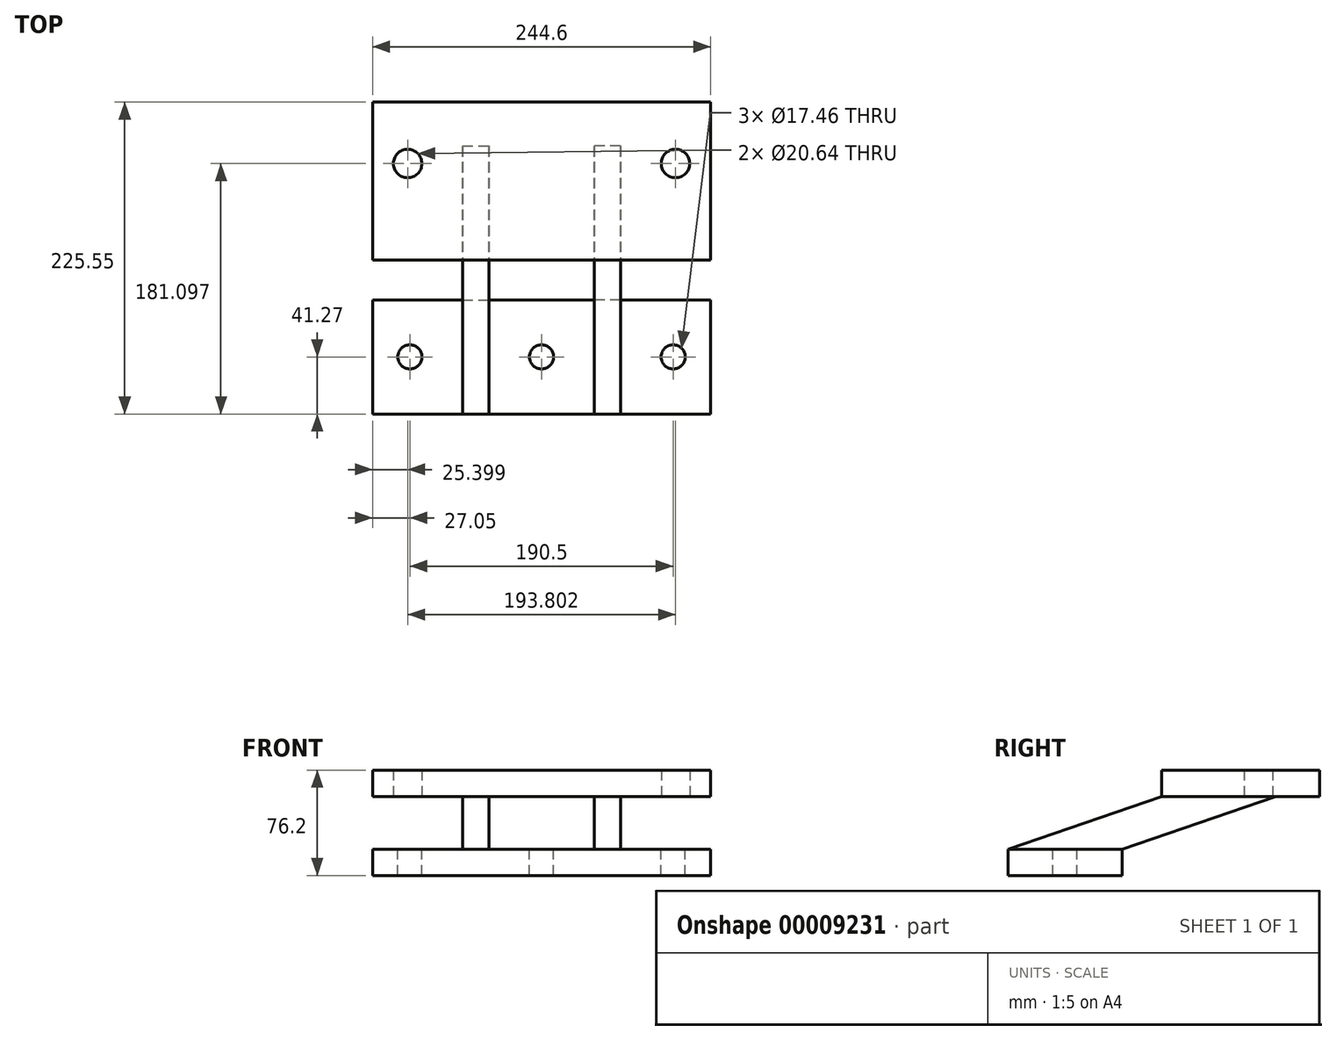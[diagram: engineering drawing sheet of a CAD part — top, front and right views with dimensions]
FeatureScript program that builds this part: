
annotation { "Feature Type Name" : "Feature", "Feature Type Description" : "" }
export const myFeature = defineFeature(function(context is Context, id is Id, definition is map)
    precondition{}
    {
        {
            var Q0;
            Q0=qCreatedBy(makeId("Top.planeOp"),FACE);
            var sketch = newSketch(context, id + "F0", { "sketchPlane" : qUnion([Q0])});
            skLineSegment(sketch, "E0.rect.bottom", {"start": v(-122.3, 41.28) * mm, "end": v(122.3, 41.28) * mm});
            skLineSegment(sketch, "E0.rect.top", {"start": v(-122.3, -41.28) * mm, "end": v(122.3, -41.28) * mm});
            skLineSegment(sketch, "E0.rect.left", {"start": v(-122.3, 41.28) * mm, "end": v(-122.3, -41.28) * mm});
            skLineSegment(sketch, "E0.rect.right", {"start": v(122.3, 41.28) * mm, "end": v(122.3, -41.28) * mm});
            skPoint(sketch, "E0.rect.middle", {"position": v(0, 0) * mm});
            skCircle(sketch, "E1", {"center": v(0, 0) * mm, "radius": 8.73 * mm});
            skCircle(sketch, "E2", {"center": v(-95.25, 0) * mm, "radius": 8.73 * mm});
            skLineSegment(sketch, "E3", {"start": v(0, 41.28) * mm, "end": v(0, -41.28) * mm, "construction": true});
            skCircle(sketch, "E4.0.MirrorC", {"center": v(95.25, 0) * mm, "radius": 8.73 * mm});
            skSolve(sketch);
        }
        {
            var Q0;
            Q0=makeQuery(id+"F0.imprint","IMPRINT",FACE,{"disambiguationData":[TD([[makeQuery(id+"F0.imprint","IMPRINT",EDGE,{"derivedFrom":sQuery(id+"F0.wireOp",EDGE,"E0.rect.bottom")}),-1.0]])]});
            extrude(context, id + "F1", {"entities" : qUnion([Q0]), "oppositeDirection" : true, "depth" : 19.05 * mm});
        }
        {
            var Q0;
            Q0=makeQuery(id+"F1.opExtrude","CAP_FACE",FACE,{"disambiguationData":[OSD([sQuery(id+"F0.wireOp",EDGE,"E0.rect.bottom"),sQuery(id+"F0.wireOp",EDGE,"E0.rect.top"),sQuery(id+"F0.wireOp",EDGE,"E0.rect.left"),sQuery(id+"F0.wireOp",EDGE,"E0.rect.right"),sQuery(id+"F0.wireOp",EDGE,"E1"),sQuery(id+"F0.wireOp",EDGE,"E2"),sQuery(id+"F0.wireOp",EDGE,"E4.0.MirrorC")])],"isStart":true});
            cPlane(context, id + "F2", {"entities" : qUnion([Q0]), "cplaneType" : CPlaneType.OFFSET, "offset" : 38.1 * mm, "width" : 152.4 * mm, "height" : 152.4 * mm});
        }
        {
            var Q0;
            Q0=qCreatedBy(id+"F2.planeOp",FACE);
            var sketch = newSketch(context, id + "F3", { "sketchPlane" : qUnion([Q0])});
            skLineSegment(sketch, "E5.0", {"start": v(-122.3, 69.98) * mm, "end": v(122.3, 69.98) * mm});
            skLineSegment(sketch, "E6.0", {"start": v(-122.3, 184.28) * mm, "end": v(122.3, 184.28) * mm});
            skLineSegment(sketch, "E7", {"start": v(-122.3, 184.28) * mm, "end": v(-122.3, 69.98) * mm});
            skLineSegment(sketch, "E8", {"start": v(122.3, 184.28) * mm, "end": v(122.3, 69.98) * mm});
            skLineSegment(sketch, "E9.0", {"start": v(-122.3, 139.83) * mm, "end": v(122.3, 139.83) * mm, "construction": true});
            skLineSegment(sketch, "E10.0", {"start": v(-96.9, 184.28) * mm, "end": v(-96.9, 69.98) * mm, "construction": true});
            skLineSegment(sketch, "E11.0", {"start": v(96.9, 184.28) * mm, "end": v(96.9, 69.98) * mm, "construction": true});
            skCircle(sketch, "E12", {"center": v(-96.9, 139.83) * mm, "radius": 10.32 * mm});
            skCircle(sketch, "E13", {"center": v(96.9, 139.83) * mm, "radius": 10.32 * mm});
            skSolve(sketch);
        }
        {
            var Q0;
            Q0 = qSketchRegion(id + "F3", true);
            extrude(context, id + "F4", {"entities" : qUnion([Q0]), "depth" : 19.05 * mm});
        }
        {
            var Q0;
            Q0=qCreatedBy(makeId("Right.planeOp"),FACE);
            var sketch = newSketch(context, id + "F5", { "sketchPlane" : qUnion([Q0])});
            skLineSegment(sketch, "E14.0.0", {"start": v(69.98, 38.1) * mm, "end": v(184.28, 38.1) * mm});
            skLineSegment(sketch, "E14.0.1", {"start": v(184.28, 38.1) * mm, "end": v(184.28, 57.15) * mm});
            skLineSegment(sketch, "E14.0.2", {"start": v(184.28, 57.15) * mm, "end": v(69.98, 57.15) * mm});
            skLineSegment(sketch, "E14.0.3", {"start": v(69.98, 57.15) * mm, "end": v(69.98, 38.1) * mm});
            skLineSegment(sketch, "E15.0.0", {"start": v(41.28, 0) * mm, "end": v(-41.28, 0) * mm});
            skLineSegment(sketch, "E15.0.1", {"start": v(-41.28, 0) * mm, "end": v(-41.28, -19.05) * mm});
            skLineSegment(sketch, "E15.0.2", {"start": v(-41.28, -19.05) * mm, "end": v(41.28, -19.05) * mm});
            skLineSegment(sketch, "E15.0.3", {"start": v(41.28, -19.05) * mm, "end": v(41.28, 0) * mm});
            skLineSegment(sketch, "E16.0", {"start": v(152.53, -19.05) * mm, "end": v(152.53, 38.1) * mm, "construction": true});
            skLineSegment(sketch, "E17", {"start": v(69.98, 38.1) * mm, "end": v(-41.28, 0) * mm});
            skLineSegment(sketch, "E18", {"start": v(41.28, 0) * mm, "end": v(152.53, 38.1) * mm});
            skSolve(sketch);
        }
        {
            var Q0;
            Q0=qCreatedBy(makeId("Right.planeOp"),FACE);
            cPlane(context, id + "F6", {"entities" : qUnion([Q0]), "cplaneType" : CPlaneType.OFFSET, "offset" : 38.1 * mm, "width" : 152.4 * mm, "height" : 152.4 * mm});
        }
        {
            var Q0;
            Q0=qCreatedBy(id+"F6.planeOp",FACE);
            var sketch = newSketch(context, id + "F7", { "sketchPlane" : qUnion([Q0])});
            skLineSegment(sketch, "E19.0.0", {"start": v(152.53, 38.1) * mm, "end": v(69.98, 38.1) * mm});
            skLineSegment(sketch, "E19.0.1", {"start": v(69.98, 38.1) * mm, "end": v(-41.28, 0) * mm});
            skLineSegment(sketch, "E19.0.2", {"start": v(-41.28, 0) * mm, "end": v(41.28, 0) * mm});
            skLineSegment(sketch, "E19.0.3", {"start": v(41.28, 0) * mm, "end": v(152.53, 38.1) * mm});
            skSolve(sketch);
        }
        {
            var Q0;
            Q0 = qSketchRegion(id + "F7", true);
            extrude(context, id + "F8", {"entities" : qUnion([Q0]), "depth" : 19.05 * mm});
        }
        {
            var Q0;
            Q0=makeQuery(id+"F8.opExtrude","SWEPT_BODY",BODY,{"disambiguationData":[OSD([sQuery(id+"F7.wireOp",EDGE,"E19.0.0"),sQuery(id+"F7.wireOp",EDGE,"E19.0.1"),sQuery(id+"F7.wireOp",EDGE,"E19.0.2"),sQuery(id+"F7.wireOp",EDGE,"E19.0.3")])]});
            var Q1;
            Q1=qCreatedBy(makeId("Right.planeOp"),FACE);
            mirror(context, id + "F9", {"entities" : qUnion([Q0]), "mirrorPlane" : qUnion([Q1])});
        }
    });
